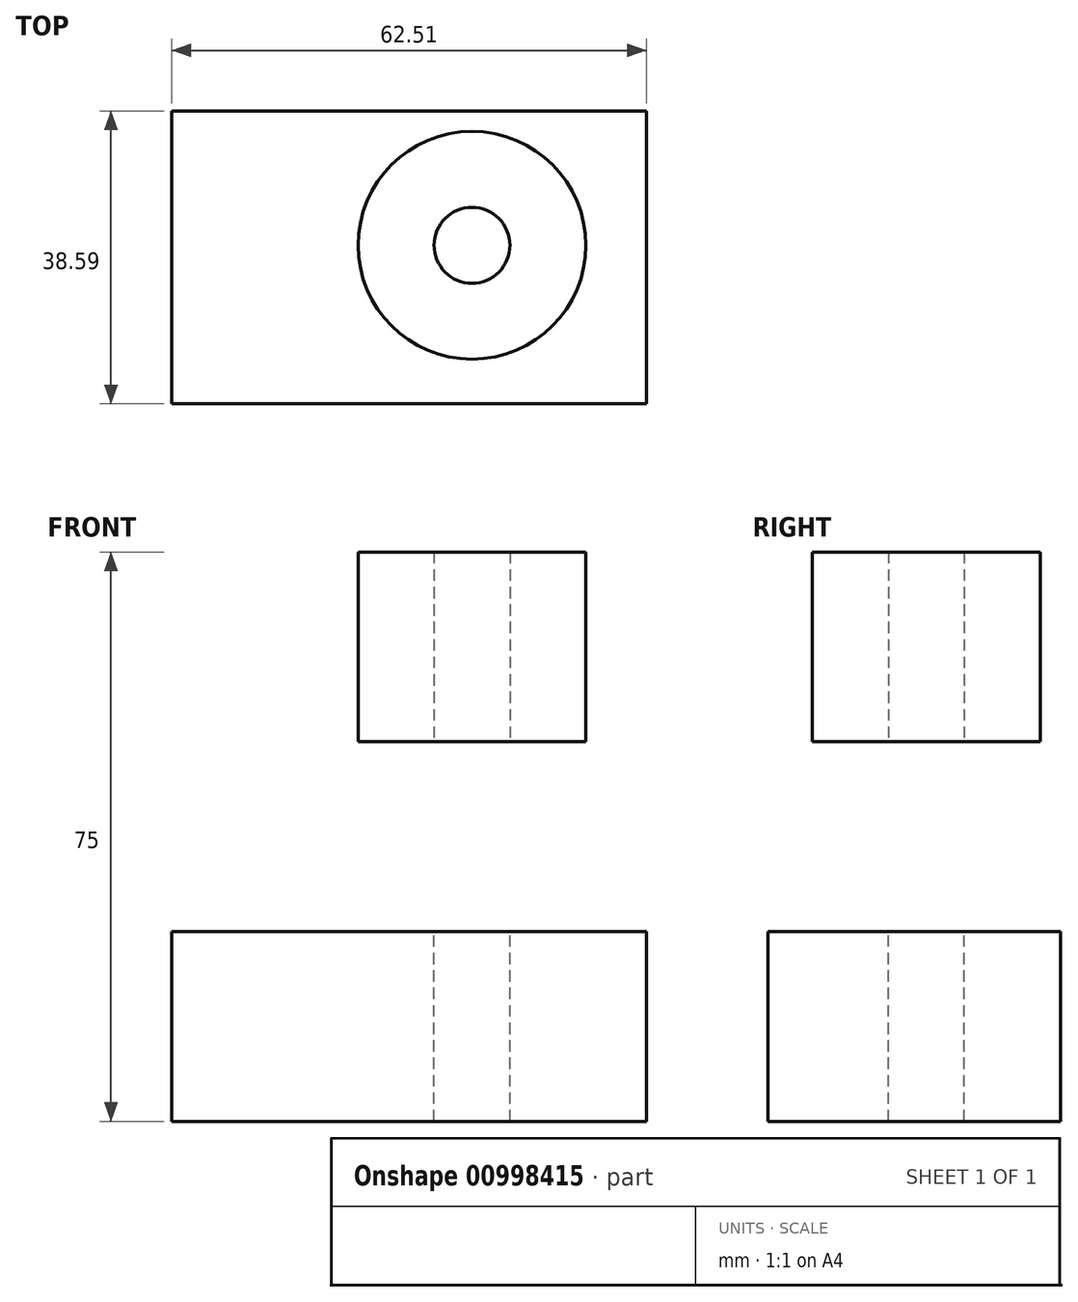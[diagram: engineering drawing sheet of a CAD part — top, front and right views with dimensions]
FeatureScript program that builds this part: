
annotation { "Feature Type Name" : "Feature", "Feature Type Description" : "" }
export const myFeature = defineFeature(function(context is Context, id is Id, definition is map)
    precondition{}
    {
        {
            var Q0;
            Q0=qCreatedBy(makeId("Top.planeOp"),FACE);
            var sketch = newSketch(context, id + "F0", { "sketchPlane" : qUnion([Q0])});
            skLineSegment(sketch, "E0.bottom", {"start": v(0, 0) * mm, "end": v(62.5, 0) * mm});
            skLineSegment(sketch, "E0.top", {"start": v(0, 38.59) * mm, "end": v(62.5, 38.59) * mm});
            skLineSegment(sketch, "E0.left", {"start": v(0, 0) * mm, "end": v(0, 38.59) * mm});
            skLineSegment(sketch, "E0.right", {"start": v(62.5, 0) * mm, "end": v(62.5, 38.59) * mm});
            skSolve(sketch);
        }
        {
            var Q0;
            Q0 = qSketchRegion(id + "F0", true);
            extrude(context, id + "F1", {"entities" : qUnion([Q0]), "depth" : 25 * mm, "offsetDistance" : 25 * mm});
        }
        {
            var Q0;
            Q0=makeQuery(id+"F1.opExtrude","CAP_FACE",FACE,{"disambiguationData":[OSD([sQuery(id+"F0.wireOp",EDGE,"E0.bottom"),sQuery(id+"F0.wireOp",EDGE,"E0.top"),sQuery(id+"F0.wireOp",EDGE,"E0.left"),sQuery(id+"F0.wireOp",EDGE,"E0.right")])],"isStart":false});
            var sketch = newSketch(context, id + "F2", { "sketchPlane" : qUnion([Q0])});
            skCircle(sketch, "E1", {"center": v(39.55, 20.89) * mm, "radius": 5 * mm});
            skSolve(sketch);
        }
        {
            var Q0;
            Q0=makeQuery(id+"F2.imprint","IMPRINT",FACE,{"disambiguationData":[TD([[makeQuery(id+"F2.imprint","IMPRINT",EDGE,{"derivedFrom":sQuery(id+"F2.wireOp",EDGE,"E1")}),1.0]])]});
            extrude(context, id + "F3", {"entities" : qUnion([Q0]), "operationType" : NewBodyOperationType.REMOVE, "oppositeDirection" : true, "depth" : 25 * mm, "offsetDistance" : 25 * mm});
        }
        {
            var Q0;
            Q0=makeQuery(id+"F1.opExtrude","CAP_FACE",FACE,{"disambiguationData":[OSD([sQuery(id+"F0.wireOp",EDGE,"E0.bottom"),sQuery(id+"F0.wireOp",EDGE,"E0.top"),sQuery(id+"F0.wireOp",EDGE,"E0.left"),sQuery(id+"F0.wireOp",EDGE,"E0.right")])],"isStart":false});
            cPlane(context, id + "F4", {"entities" : qUnion([Q0]), "cplaneType" : CPlaneType.OFFSET, "offset" : 25 * mm, "width" : 150 * mm, "height" : 150 * mm});
        }
        {
            var Q0;
            Q0=qCreatedBy(id+"F4.planeOp",FACE);
            var sketch = newSketch(context, id + "F5", { "sketchPlane" : qUnion([Q0])});
            skCircle(sketch, "E2.0", {"center": v(39.55, 20.89) * mm, "radius": 5 * mm});
            skCircle(sketch, "E3.0", {"center": v(39.55, 20.89) * mm, "radius": 15 * mm});
            skSolve(sketch);
        }
        {
            var Q0;
            Q0=makeQuery(id+"F5.imprint","IMPRINT",FACE,{"disambiguationData":[TD([[makeQuery(id+"F5.imprint","IMPRINT",EDGE,{"derivedFrom":sQuery(id+"F5.wireOp",EDGE,"E2.0")}),-1.0]])]});
            extrude(context, id + "F6", {"entities" : qUnion([Q0]), "depth" : 25 * mm, "offsetDistance" : 25 * mm});
        }
        {
            var Q0;
            Q0=qCreatedBy(makeId("Top.planeOp"),FACE);
            cPlane(context, id + "F7", {"entities" : qUnion([Q0]), "cplaneType" : CPlaneType.OFFSET, "offset" : 10 * mm, "width" : 150 * mm, "height" : 150 * mm});
        }
    });
